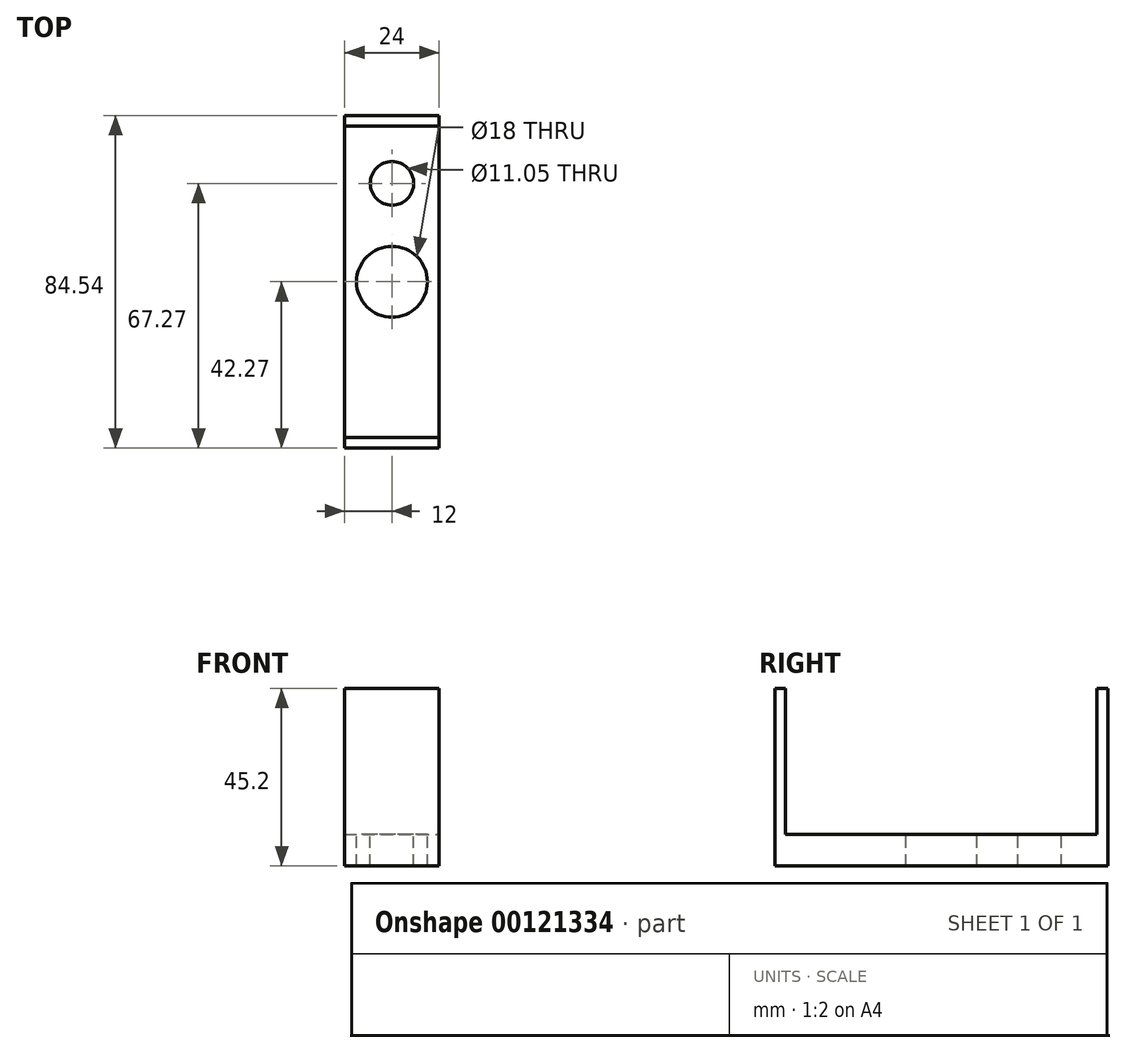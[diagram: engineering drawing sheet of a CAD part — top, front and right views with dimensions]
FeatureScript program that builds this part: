
annotation { "Feature Type Name" : "Feature", "Feature Type Description" : "" }
export const myFeature = defineFeature(function(context is Context, id is Id, definition is map)
    precondition{}
    {
        {
            var Q0;
            Q0=qCreatedBy(makeId("Top.planeOp"),FACE);
            var sketch = newSketch(context, id + "F0", { "sketchPlane" : qUnion([Q0])});
            skLineSegment(sketch, "E0.bottom", {"start": v(-12, 42.27) * mm, "end": v(12, 42.27) * mm});
            skLineSegment(sketch, "E0.top", {"start": v(-12, -42.27) * mm, "end": v(12, -42.27) * mm});
            skLineSegment(sketch, "E0.left", {"start": v(-12, 42.27) * mm, "end": v(-12, -42.27) * mm});
            skLineSegment(sketch, "E0.right", {"start": v(12, 42.27) * mm, "end": v(12, -42.27) * mm});
            skSolve(sketch);
        }
        {
            var Q0;
            Q0 = qSketchRegion(id + "F0", true);
            extrude(context, id + "F1", {"entities" : qUnion([Q0]), "depth" : 8 * mm});
        }
        {
            var Q0;
            Q0=makeQuery(id+"F1.opExtrude","CAP_FACE",FACE,{"disambiguationData":[OSD([sQuery(id+"F0.wireOp",EDGE,"E0.bottom"),sQuery(id+"F0.wireOp",EDGE,"E0.top"),sQuery(id+"F0.wireOp",EDGE,"E0.left"),sQuery(id+"F0.wireOp",EDGE,"E0.right")])],"isStart":false});
            var sketch = newSketch(context, id + "F2", { "sketchPlane" : qUnion([Q0])});
            skLineSegment(sketch, "E1.bottom", {"start": v(-12, 42.27) * mm, "end": v(12, 42.27) * mm});
            skLineSegment(sketch, "E1.top", {"start": v(-12, 39.57) * mm, "end": v(12, 39.57) * mm});
            skLineSegment(sketch, "E1.left", {"start": v(-12, 42.27) * mm, "end": v(-12, 39.57) * mm});
            skLineSegment(sketch, "E1.right", {"start": v(12, 42.27) * mm, "end": v(12, 39.57) * mm});
            skLineSegment(sketch, "E2.bottom", {"start": v(-12, -39.57) * mm, "end": v(12, -39.57) * mm});
            skLineSegment(sketch, "E2.top", {"start": v(-12, -42.27) * mm, "end": v(12, -42.27) * mm});
            skLineSegment(sketch, "E2.left", {"start": v(-12, -39.57) * mm, "end": v(-12, -42.27) * mm});
            skLineSegment(sketch, "E2.right", {"start": v(12, -39.57) * mm, "end": v(12, -42.27) * mm});
            skSolve(sketch);
        }
        {
            var Q0;
            Q0 = qSketchRegion(id + "F2", true);
            extrude(context, id + "F3", {"entities" : qUnion([Q0]), "operationType" : NewBodyOperationType.ADD, "depth" : 37.2 * mm});
        }
        {
            var Q0;
            Q0=makeQuery(id+"F1.opExtrude","CAP_FACE",FACE,{"disambiguationData":[OSD([sQuery(id+"F0.wireOp",EDGE,"E0.bottom"),sQuery(id+"F0.wireOp",EDGE,"E0.top"),sQuery(id+"F0.wireOp",EDGE,"E0.left"),sQuery(id+"F0.wireOp",EDGE,"E0.right")])],"isStart":false});
            var sketch = newSketch(context, id + "F4", { "sketchPlane" : qUnion([Q0])});
            skCircle(sketch, "E3", {"center": v(0, 0) * mm, "radius": 9 * mm});
            skSolve(sketch);
        }
        {
            var Q0;
            Q0 = qSketchRegion(id + "F4", true);
            extrude(context, id + "F5", {"entities" : qUnion([Q0]), "operationType" : NewBodyOperationType.REMOVE, "endBound" : BoundingType.THROUGH_ALL, "oppositeDirection" : true, "depth" : 25 * mm});
        }
        {
            var Q0;
            Q0=makeQuery(id+"F1.opExtrude","CAP_FACE",FACE,{"disambiguationData":[OSD([sQuery(id+"F0.wireOp",EDGE,"E0.bottom"),sQuery(id+"F0.wireOp",EDGE,"E0.top"),sQuery(id+"F0.wireOp",EDGE,"E0.left"),sQuery(id+"F0.wireOp",EDGE,"E0.right")])],"isStart":false});
            var sketch = newSketch(context, id + "F6", { "sketchPlane" : qUnion([Q0])});
            skCircle(sketch, "E4", {"center": v(0, 25) * mm, "radius": 5.52 * mm});
            skSolve(sketch);
        }
        {
            var Q0;
            Q0 = qSketchRegion(id + "F6", true);
            extrude(context, id + "F7", {"entities" : qUnion([Q0]), "operationType" : NewBodyOperationType.REMOVE, "endBound" : BoundingType.THROUGH_ALL, "oppositeDirection" : true, "depth" : 25 * mm});
        }
    });
